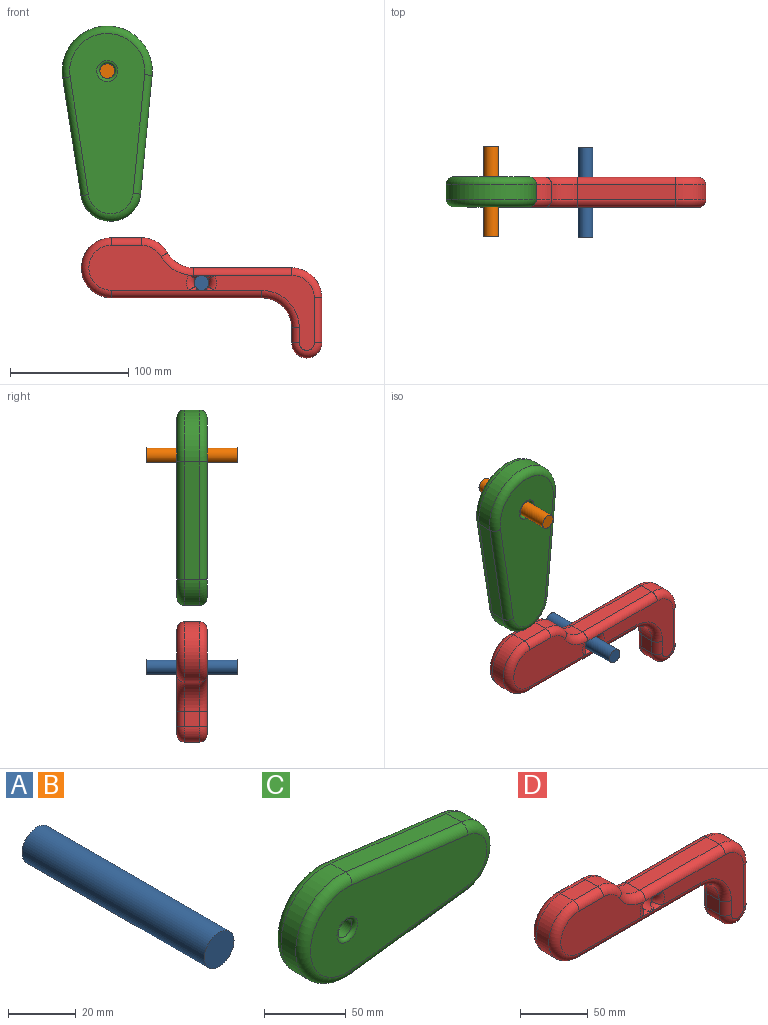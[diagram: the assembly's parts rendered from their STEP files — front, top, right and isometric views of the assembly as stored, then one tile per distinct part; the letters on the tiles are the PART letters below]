
ASSEMBLY  parts=4 mates=2
PART A: 3 faces, bbox 12.4x76.2x12.4 mm
  f0: cylinder r=6.22mm len=76.2mm, axis (0,1,0), area 2979.4mm2, adj f1,f2
  f1: plane 12.45x12.45mm, normal (0,-1,0), area 121.7mm2, adj f0
  f2: plane 12.45x12.45mm, normal (0,1,0), area 121.7mm2, adj f0
PART B: same geometry as A
PART C: 17 faces, bbox 170.3x25.4x82.5 mm
  f0: plane 100.01x12.7mm, normal (0.12,0,0.99), area 1280.2mm2, adj f1,f3,f7,f11
  f1: cylinder r=38.1mm len=76.2mm, axis (0,1,0), area 1641.4mm2, adj f0,f2,f8,f12
  f2: plane 100.01x12.7mm, normal (0.12,0,-0.99), area 1280.2mm2, adj f1,f3,f10,f14
  f3: cylinder r=25.4mm len=50.4mm, axis (0,1,0), area 932.6mm2, adj f0,f2,f9,f13
  f4: cylinder r=6.35mm len=20.32mm, axis (0,1,0), area 810.7mm2, adj f15,f16
  f5: plane 152.4x63.5mm, normal (0,-1,0), area 7106.9mm2, adj f11,f12,f13,f14,f16
  f6: plane 152.4x63.5mm, normal (0,1,0), area 7106.9mm2, adj f7,f8,f9,f10,f15
  f7: cylinder r=6.35mm len=100.81mm, axis (-0.99,0,0.12), area 1005.5mm2, adj f0,f6,f8,f9
  f8: torus R=31.75mm, axis (0,-1,0), area 1211.1mm2, adj f1,f6,f7,f10
  f9: torus R=19.05mm, axis (0,-1,0), area 665.9mm2, adj f3,f6,f7,f10
  f10: cylinder r=6.35mm len=100.81mm, axis (0.99,0,0.12), area 1005.5mm2, adj f2,f6,f8,f9
  f11: cylinder r=6.35mm len=100.81mm, axis (0.99,0,-0.12), area 1005.5mm2, adj f0,f5,f12,f13
  f12: torus R=31.75mm, axis (0,-1,0), area 1211.1mm2, adj f1,f5,f11,f14
  f13: torus R=19.05mm, axis (0,-1,0), area 665.9mm2, adj f3,f5,f11,f14
  f14: cylinder r=6.35mm len=100.81mm, axis (-0.99,0,-0.12), area 1005.5mm2, adj f2,f5,f12,f13
  f15: torus R=8.89mm, axis (0,-1,0), area 182.3mm2, adj f4,f6
  f16: torus R=8.89mm, axis (0,-1,0), area 182.3mm2, adj f4,f5
PART D: 52 faces, bbox 207.4x26x104.7 mm
  f0: plane 84.4x38.1mm, normal (0,-1,0), area 2528.6mm2, adj f29,f31,f33,f35,f37,f39
  f1: plane 84.25x63.5mm, normal (0,1,0), area 1821.7mm2, adj f16,f17,f19,f21,f23,f25,f26,f47
  f2: plane 83.01x12.7mm, normal (0,0,1), area 1054.2mm2, adj f13,f15,f16,f27
  f3: plane 38.1x12.7mm, normal (1,0,0), area 483.9mm2, adj f12,f13,f19,f30
  f4: plane 127x12.7mm, normal (0,0,-1), area 1612.9mm2, adj f9,f14,f26,f37
  f5: cylinder r=6.35mm len=25.4mm, axis (0,1,0), area 636.8mm2, adj f38,f39,f40,f41,f42,f43,f44,f45
  f6: plane 84.25x63.5mm, normal (0,-1,0), area 1821.7mm2, adj f27,f28,f30,f32,f34,f36,f37,f50
  f7: plane 84.4x38.1mm, normal (0,1,0), area 2528.6mm2, adj f18,f20,f22,f24,f26,f43
  f8: plane 25.4x12.7mm, normal (0,0,1), area 322.6mm2, adj f9,f10,f22,f33
  f9: cylinder r=25.4mm len=50.8mm, axis (0,1,0), area 1013.4mm2, adj f4,f8,f24,f35
  f10: cylinder r=25.4mm len=22mm, axis (0,1,0), area 337.8mm2, adj f8,f15,f20,f31
  f11: plane 12.7x12.7mm, normal (-1,0,0), area 161.3mm2, adj f12,f14,f23,f34
  f12: cylinder r=12.7mm len=25.4mm, axis (0,1,0), area 506.7mm2, adj f3,f11,f21,f32
  f13: cylinder r=25.4mm len=25.4mm, axis (0,-1,0), area 506.7mm2, adj f2,f3,f17,f28
  f14: cylinder r=25.4mm len=25.4mm, axis (0,1,0), area 506.7mm2, adj f4,f11,f25,f36
  f15: cylinder r=25.4mm len=22mm, axis (0,1,0), area 337.8mm2, adj f2,f10,f18,f29
  f16: cylinder r=6.35mm len=83.01mm, axis (-1,0,0), area 827.9mm2, adj f1,f2,f17,f18,f45,f46
  f17: torus R=19.05mm, axis (0,-1,0), area 361.8mm2, adj f1,f13,f16,f19
  f18: torus R=31.75mm, axis (0,-1,0), area 289.4mm2, adj f7,f15,f16,f20,f44
  f19: cylinder r=6.35mm len=38.1mm, axis (0,0,1), area 380mm2, adj f1,f3,f17,f21
  f20: torus R=19.05mm, axis (0,-1,0), area 241.2mm2, adj f7,f10,f18,f22
  f21: torus R=6.35mm, axis (0,-1,0), area 325.7mm2, adj f1,f12,f19,f23
  f22: cylinder r=6.35mm len=25.4mm, axis (-1,0,0), area 253.4mm2, adj f7,f8,f20,f24
  f23: cylinder r=6.35mm len=12.7mm, axis (0,0,-1), area 126.7mm2, adj f1,f11,f21,f25
  f24: torus R=19.05mm, axis (0,-1,0), area 723.6mm2, adj f7,f9,f22,f26
  f25: torus R=31.75mm, axis (0,-1,0), area 434.1mm2, adj f1,f14,f23,f26
  f26: cylinder r=6.35mm len=127mm, axis (1,0,0), area 1266.8mm2, adj f1,f4,f7,f24,f25,f42,f48
  f27: cylinder r=6.35mm len=83.01mm, axis (1,0,0), area 827.9mm2, adj f2,f6,f28,f29,f41,f49
  f28: torus R=19.05mm, axis (0,-1,0), area 361.8mm2, adj f6,f13,f27,f30
  f29: torus R=31.75mm, axis (0,-1,0), area 289.4mm2, adj f0,f15,f27,f31,f40
  f30: cylinder r=6.35mm len=38.1mm, axis (0,0,-1), area 380mm2, adj f3,f6,f28,f32
  f31: torus R=19.05mm, axis (0,-1,0), area 241.2mm2, adj f0,f10,f29,f33
  f32: torus R=6.35mm, axis (0,-1,0), area 325.7mm2, adj f6,f12,f30,f34
  f33: cylinder r=6.35mm len=25.4mm, axis (1,0,0), area 253.4mm2, adj f0,f8,f31,f35
  f34: cylinder r=6.35mm len=12.7mm, axis (0,0,1), area 126.7mm2, adj f6,f11,f32,f36
  f35: torus R=19.05mm, axis (0,-1,0), area 723.6mm2, adj f0,f9,f33,f37
  f36: torus R=31.75mm, axis (0,-1,0), area 434.1mm2, adj f6,f14,f34,f37
  f37: cylinder r=6.35mm len=127mm, axis (-1,0,0), area 1266.8mm2, adj f0,f4,f6,f35,f36,f38,f51
  f38: bspline ~11.38x6.67mm, area 35.8mm2, adj f5,f37,f39
  f39: torus R=12.7mm, axis (0,-1,0), area 92.5mm2, adj f0,f5,f38,f40
  f40: bspline ~7.67x6.4mm, area 18.4mm2, adj f5,f29,f39,f41
  f41: bspline ~7.6x5.07mm, area 14.2mm2, adj f5,f27,f40
  f42: bspline ~11.38x6.67mm, area 35.8mm2, adj f5,f26,f43
  f43: torus R=12.7mm, axis (0,-1,0), area 92.5mm2, adj f5,f7,f42,f44
  f44: bspline ~7.44x6.35mm, area 18.5mm2, adj f5,f18,f43,f45
  f45: bspline ~7.6x5.07mm, area 14.4mm2, adj f5,f16,f44
  f46: bspline ~11.38x6.67mm, area 35.8mm2, adj f5,f16,f47
  f47: torus R=12.7mm, axis (0,-1,0), area 90.4mm2, adj f1,f5,f46,f48
  f48: bspline ~11.38x6.67mm, area 35.8mm2, adj f5,f26,f47
  f49: bspline ~11.38x6.67mm, area 35.8mm2, adj f5,f27,f50
  f50: torus R=12.7mm, axis (0,-1,0), area 90.4mm2, adj f5,f6,f49,f51
  f51: bspline ~11.38x6.67mm, area 35.8mm2, adj f5,f37,f50
PLACE A t=(79.75,0,-179.01)mm
PLACE B at identity fixed
PLACE C rot(axis=(0,1,0),88.4deg) t=(0.45,-25.4,-52.95)mm
PLACE D t=(79.75,-25.4,-179.01)mm
MATE revolute A.f0 <-> D.f5  axis (0,1,0) through (79.75,-38.1,-179.01)mm
MATE revolute B.f0 <-> C.f1  axis (0,1,0) through (0,-38.1,0)mm
